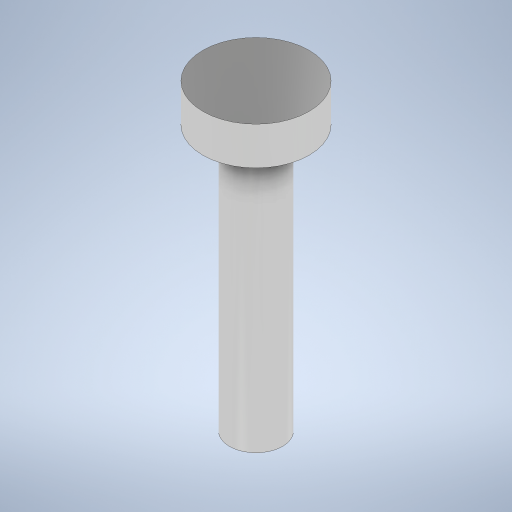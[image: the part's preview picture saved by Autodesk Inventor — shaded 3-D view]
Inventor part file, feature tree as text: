
AUTODESK INVENTOR PART (.ipt)
format: ipt  version: 2024 (Build 280153000, 153)  size: 239,104 bytes
history: native  units: mm
features: extrude x2, sketch x2
ambient origin geometry x8: Origin, YZ Plane, XZ Plane, XY Plane, X Axis, Y Axis, Z Axis, Center Point
bodies: Solid1 (feature_tree)
feature tree (4):
  extrude  "Extrusion1"  Depth=2.5mm TaperAngle=0.0deg
  extrude  "Extrusion2"  Depth=17.5mm TaperAngle=0.0deg
  sketch  "Sketch1"  dims[d0=7.0mm d1=2.5mm d2=0.0mm]
  sketch  "Sketch2"  dims[d3=3.5mm d4=17.5mm d5=0.0mm]
